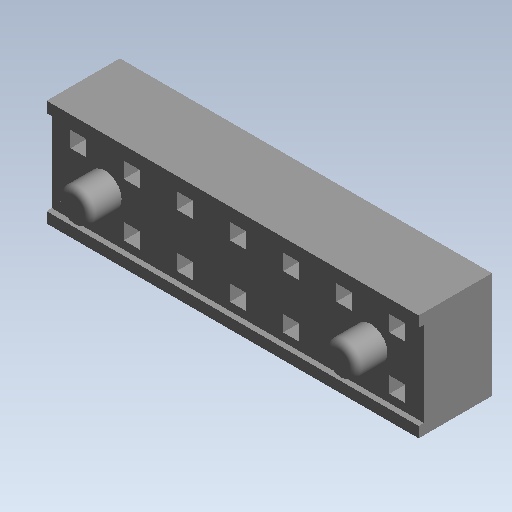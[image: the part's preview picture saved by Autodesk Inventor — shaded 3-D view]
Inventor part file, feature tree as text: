
AUTODESK INVENTOR PART (.ipt)
format: ipt  version: 2021 (Build 250183000, 183)  size: 221,184 bytes
history: native  units: mm (DEFAULTED — no unit token found)
features: other x14, sketch x5, extrude x3, revolve x2, pattern_linear x1
ambient origin geometry x8: Origin, YZ Plane, XZ Plane, XY Plane, X Axis, Y Axis, Z Axis, Center Point
bodies: Solid1 (feature_tree)
feature tree (25):
  extrude  "Extrusion1"  Depth=17.78mm TaperAngle=0.0deg
  extrude  "Extrusion2"  TaperAngle=360.0deg  [1 undecoded]
  revolve  "Revolution1"  [1 undecoded]
  revolve  "Revolution2"  [1 undecoded]
  extrude  "Extrusion3"  [1 undecoded]
  pattern_linear  "Rectangular Pattern1"  [2 undecoded]
  other  "socket_to_dummy_XY"
  other  "socket_to_dummy_YZ"
  other  "socket_to_dummy_ZX"
  other  "socket_to_dummy_X"
  other  "socket_to_dummy_Y"
  other  "socket_to_dummy_Z"
  other  "socket_to_dummy_Center"
  other  "socket_to_pad_XY"
  other  "socket_to_pad_YZ"
  other  "socket_to_pad_ZX"
  other  "socket_to_pad_X"
  other  "socket_to_pad_Y"
  other  "socket_to_pad_Z"
  other  "socket_to_pad_Center"
  sketch  "Sketch_1"  dims[d0=3.5052mm d1=0.0mm d2=17.78mm d3=0.0mm]
  sketch  "Sketch_4"  dims[d4=360.0deg d5=360.0deg]
  sketch  "Sketch_9"  dims[d6=1.27mm d7=0.0mm d8=60.0mm d10=2.54mm d11=10.0mm d13=0.0mm]
  sketch  "Sketch_10"  dims[d14=0.0mm]
  sketch  "Sketch_11"
note: 6 required parameter values undecoded (feature->parameter linkage not recoverable at this tier; creation-order binding heuristic only, values carry confidence <= 0.55)